# Revit family: Lighting Fixture_Sylvania_Expospot 90 Fixed_Ceiling Recessed1
name_source: partatom
category: Lighting Fixtures
revit_build: Autodesk Revit 2016 (Build: 20161004_0715(x64)
units: mm (PartAtom-declared; Revit-internal decimal feet)

## family parameters
Cut with Voids When Loaded = No
Host = Face
Light Source = Yes
OmniClass Number = 23.80.70.11.17
OmniClass Title = Specialized Lighting by Location or Use
Part Type = Normal
Room Calculation Point = No
Round Connector Dimension = Use Diameter
Shared = No

## types (24) — shared parameters
Apparent Load = 28 VA
Assembly Code = D5020200
Average Life = 50 000h
Body Material = Aluminum_Sylvania_Expospot_White
Color Filter = 16777215
Colour Variation Initial = 3SDCM
Control Gear Mounting = Remote
Control Gear Required = No
Control Gear Type = Electronic
Cooling Big Axis = 43 mm  [stored 0.141076 ft]
Cooling Material = Plastic_Sylvania_Expospot_Black
Cooling Small Axis = 43 mm  [stored 0.141076 ft]
Cutout Diameter = 113 mm
Description = Specifically designed for Retail and Display applications. I.e. Supermarkets, Fashion Retail, Department stores. Build around a 90mm reflector and lens combination.
Diameter = 123 mm  [stored 0.403543 ft]
Dimmable = N
Dimming Lamp Color Temperature Shift = <None>
Drive Current = 700mA
Electrical Protection = Class II
Emit Shape Visible in Rendering = No
Emit from Circle Diameter = 99 mm  [stored 0.324803 ft]
Glow Wire Test = 850 °C
Height = 104 mm  [stored 0.341207 ft]
IK Rating = IK02
IP Rating = IP20
Inrush Current = 19 A
Inrush Duration = 250µs
LOR = 100%
Lamp = LED
Manufacturer = Feilo Sylvania
Max. Luminaires per 10A B Breaker = 13
Max. Luminaires per 10A C Breaker = 21
Max. Luminaires per 13A B Breaker = 17
Max. Luminaires per 13A C Breaker = 28
Max. Luminaires per 16A B Breaker = 21
Max. Luminaires per 16A C Breaker = 35
Max. Luminaires per 20A B Breaker = 27
Max. Luminaires per 20A C Breaker = 45
Nominal Frequency = 50/60Hz
Photobiological Risk Group = RG1
Product Family = EXPOSPOT 90 FIXED
Product Page URL = http://www.sylvania-lighting.com
Radius = 61.5 mm  [stored 0.201772 ft]
Reflector Material = Aluminum_Sylvania_Expospot_Polished
Tilt Angle = -90°
URL = http://www.sylvania-lighting.com
Voltage = 240 V
Voltage Comments = 220-240V~
Weight = 1 kg
zero-valued in all types: Default Elevation

## per-type parameters (varying)
| type | Beam Angle | CRI | Diffuser Material | Lamp Power Factor | Photometric Web File | Product Code | Total Power Consumption |
| EXPOSPOT 90 FIX HE 90 4K WB WH | 57° | 90Ra | Acrylic_Sylvania_Expospot_4000K | 0.92 | 0060260.ies | 0060260 | 28 W |
| EXPOSPOT 90 FIX HE 90 4K MB WH | 45° | 90Ra | Acrylic_Sylvania_Expospot_4000K | 0.92 | 0060259.ies | 0060259 | 28 W |
| EXPOSPOT 90 FIX HE 90 4K NB WH | 26° | 90Ra | Acrylic_Sylvania_Expospot_4000K | 0.92 | 0060258.ies | 0060258 | 28 W |
| EXPOSPOT 90 FIX HE 90 3K WB WH | 58° | 90Ra | Acrylic_Sylvania_Expospot_3000K | 0.92 | 0060257.ies | 0060257 | 28 W |
| EXPOSPOT 90 FIX HE 90 3K MB WH | 44° | 90Ra | Acrylic_Sylvania_Expospot_3000K | 0.92 | 0060256.ies | 0060256 | 28 W |
| EXPOSPOT 90 FIX HE 90 3K NB WH | 25° | 90Ra | Acrylic_Sylvania_Expospot_3000K | 0.92 | 0060255.ies | 0060255 | 28 W |
| EXPOSPOT 90 FIX HE 80 4K WB WH | 57° | 80Ra | Acrylic_Sylvania_Expospot_4000K | 0.92 | 0060254.ies | 0060254 | 28 W |
| EXPOSPOT 90 FIX HE 80 4K MB WH | 43° | 80Ra | Acrylic_Sylvania_Expospot_4000K | 0.92 | 0060253.ies | 0060253 | 28 W |
| EXPOSPOT 90 FIX HE 80 4K NB WH | 29° | 80Ra | Acrylic_Sylvania_Expospot_4000K | 0.92 | 0060252.ies | 0060252 | 28 W |
| EXPOSPOT 90 FIX HE 80 3K WB WH | 61° | 80Ra | Acrylic_Sylvania_Expospot_3000K | 0.92 | 0060251.ies | 0060251 | 28 W |
| EXPOSPOT 90 FIX HE 80 3K MB WH | 47° | 80Ra | Acrylic_Sylvania_Expospot_3000K | 0.92 | 0060250.ies | 0060250 | 28 W |
| EXPOSPOT 90 FIX HE 80 3K NB WH | 26° | 80Ra | Acrylic_Sylvania_Expospot_3000K | 0.92 | 0060249.ies | 0060249 | 28 W |
| EXPOSPOT 90 FIX HO 90 4K WB WH | 57° | 90Ra | Acrylic_Sylvania_Expospot_4000K | 0.95 | 0060284.ies | 0060284 | 35 W |
| EXPOSPOT 90 FIX HO 90 4K MB WH | 43° | 90Ra | Acrylic_Sylvania_Expospot_4000K | 0.95 | 0060283.ies | 0060283 | 35 W |
| EXPOSPOT 90 FIX HO 90 4K NB WH | 26° | 90Ra | Acrylic_Sylvania_Expospot_4000K | 0.95 | 0060282.ies | 0060282 | 35 W |
| EXPOSPOT 90 FIX HO 90 3K WB WH | 56° | 90Ra | Acrylic_Sylvania_Expospot_3000K | 0.95 | 0060281.ies | 0060281 | 35 W |
| EXPOSPOT 90 FIX HO 90 3K MB WH | 44° | 90Ra | Acrylic_Sylvania_Expospot_3000K | 0.95 | 0060280.ies | 0060280 | 35 W |
| EXPOSPOT 90 FIX HO 90 3K NB WH | 26° | 90Ra | Acrylic_Sylvania_Expospot_3000K | 0.95 | 0060279.ies | 0060279 | 35 W |
| EXPOSPOT 90 FIX HO 80 4K WB WH | 60° | 80Ra | Acrylic_Sylvania_Expospot_4000K | 0.95 | 0060278.ies | 0060278 | 35 W |
| EXPOSPOT 90 FIX HO 80 4K MB WH | 43° | 80Ra | Acrylic_Sylvania_Expospot_4000K | 0.95 | 0060277.ies | 0060277 | 35 W |
| EXPOSPOT 90 FIX HO 80 4K NB WH | 27° | 80Ra | Acrylic_Sylvania_Expospot_4000K | 0.95 | 0060276.ies | 0060276 | 35 W |
| EXPOSPOT 90 FIX HO 80 3K WB WH | 62° | 80Ra | Acrylic_Sylvania_Expospot_3000K | 0.95 | 0060275.ies | 0060275 | 35 W |
| EXPOSPOT 90 FIX HO 80 3K MB WH | 45° | 80Ra | Acrylic_Sylvania_Expospot_3000K | 0.95 | 0060274.ies | 0060274 | 35 W |
| EXPOSPOT 90 FIX HO 80 3K NB WH | 27° | 80Ra | Acrylic_Sylvania_Expospot_3000K | 0.95 | 0060273.ies | 0060273 | 35 W |

note: column(s) folded — value = type name in every type: Model

note: [stored X ft] marks values corroborated as IEEE doubles in the binary element streams (Revit-internal decimal feet)

## geometry (parser evidence)
native form markers: Sweep x3
no freeform markers — native parametric forms only
